# Revit family: STH9618_30_40_65
name_source: partatom
category: Luminárias
units: mm (PartAtom-declared; Revit-internal decimal feet)

## family parameters
Com base no plano de trabalho = Não
Compartilhado = Não
Corte com vazios quando carregada = Não
Cota do conector redondo = Utilizar diâmetro
Fonte luminosa = Sim
Manter orientação da anotação = Não
Ponto de cálculo do ambiente = Não
Sempre na vertical = Sim
Tipo de parte = Normal

## types (3) — shared parameters
Comprimento = 1.16 m
Dimerização = Não dimerizável
Diâmetro = 0.02 m
Estrutura = Al - Branco
Fabricante = Stella
Filtro de cor = 16777215
Grau de proteção (IP) = IP20
IRC (Índice de reprodução de cores) = >80
Modelo = Tubular T5 115cm
Potência = 18 W
Tensão Elétrica = 100V-240V
Troca de temperatura da cor de lâmpada com esmaecimento = <Nenhum>
URL = https://stella.com.br
Ângulo de Abertura = 160°
Ângulo de inclinação = 90.00°
zero-valued in all types: Elevação padrão

## per-type parameters (varying)
| type | Arquivo de rede fotométrica | Fluxo Luminoso | Luminoso | Referência | Temperatura da cor (K) |
| STH9618/30 - BIVOLT - 3000K - 1900lm - 160° | STELLA - STH9618-30 - TUBULAR T5 18W.ies | 1900 lm | Luminoso - 3000K | STH9618/30 - BIVOLT | 3000 K |
| STH9618/40 - BIVOLT - 4000K - 2000lm - 160° | STELLA - STH9618-40 - TUBULAR T5 18W.ies | 2000 lm | Luminoso - 4000K | STH9618/40 - BIVOLT | 4000 K |
| STH9618/65 - BIVOLT - 6500K - 2000lm - 160° | STELLA - STH9618-65 - TUBULAR T5 18W.ies | 2000 lm | Luminoso - 6500K | STH9618/65 - BIVOLT | 6500 K |
